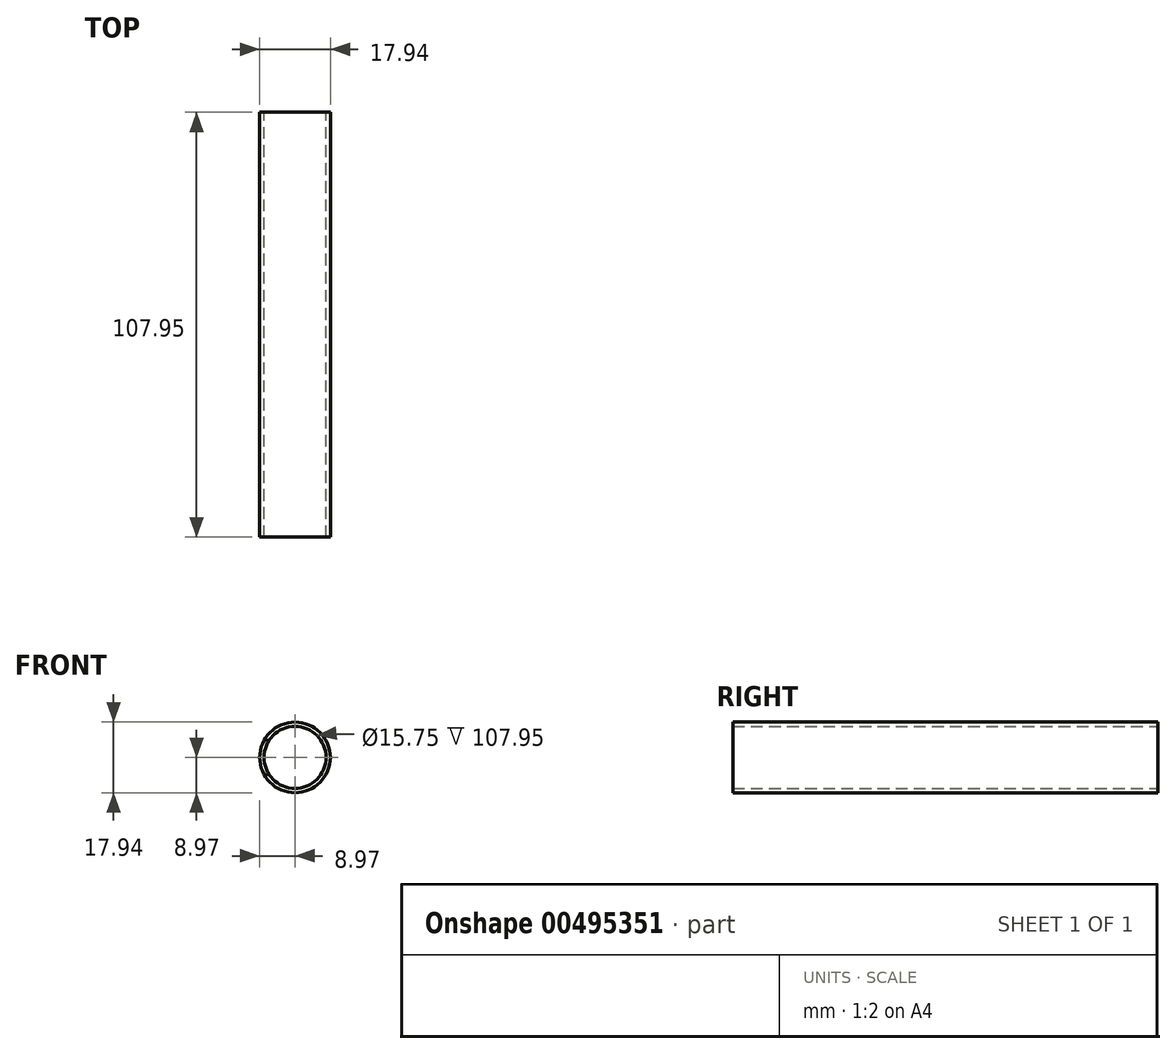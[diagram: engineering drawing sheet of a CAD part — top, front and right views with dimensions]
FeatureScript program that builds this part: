
annotation { "Feature Type Name" : "Feature", "Feature Type Description" : "" }
export const myFeature = defineFeature(function(context is Context, id is Id, definition is map)
    precondition{}
    {
        {
            var Q0;
            Q0=qCreatedBy(makeId("Front.planeOp"),FACE);
            var sketch = newSketch(context, id + "F0", { "sketchPlane" : qUnion([Q0])});
            skCircle(sketch, "E0", {"center": v(0, 0) * mm, "radius": 8.97 * mm});
            skCircle(sketch, "E1", {"center": v(0, 0) * mm, "radius": 7.87 * mm});
            skSolve(sketch);
        }
        {
            var Q0;
            Q0=makeQuery(id+"F0.imprint","IMPRINT",FACE,{"disambiguationData":[TD([[makeQuery(id+"F0.imprint","IMPRINT",EDGE,{"derivedFrom":sQuery(id+"F0.wireOp",EDGE,"E0")}),1.0]])]});
            extrude(context, id + "F1", {"entities" : qUnion([Q0]), "depth" : 107.95 * mm, "offsetDistance" : 25.4 * mm});
        }
    });
